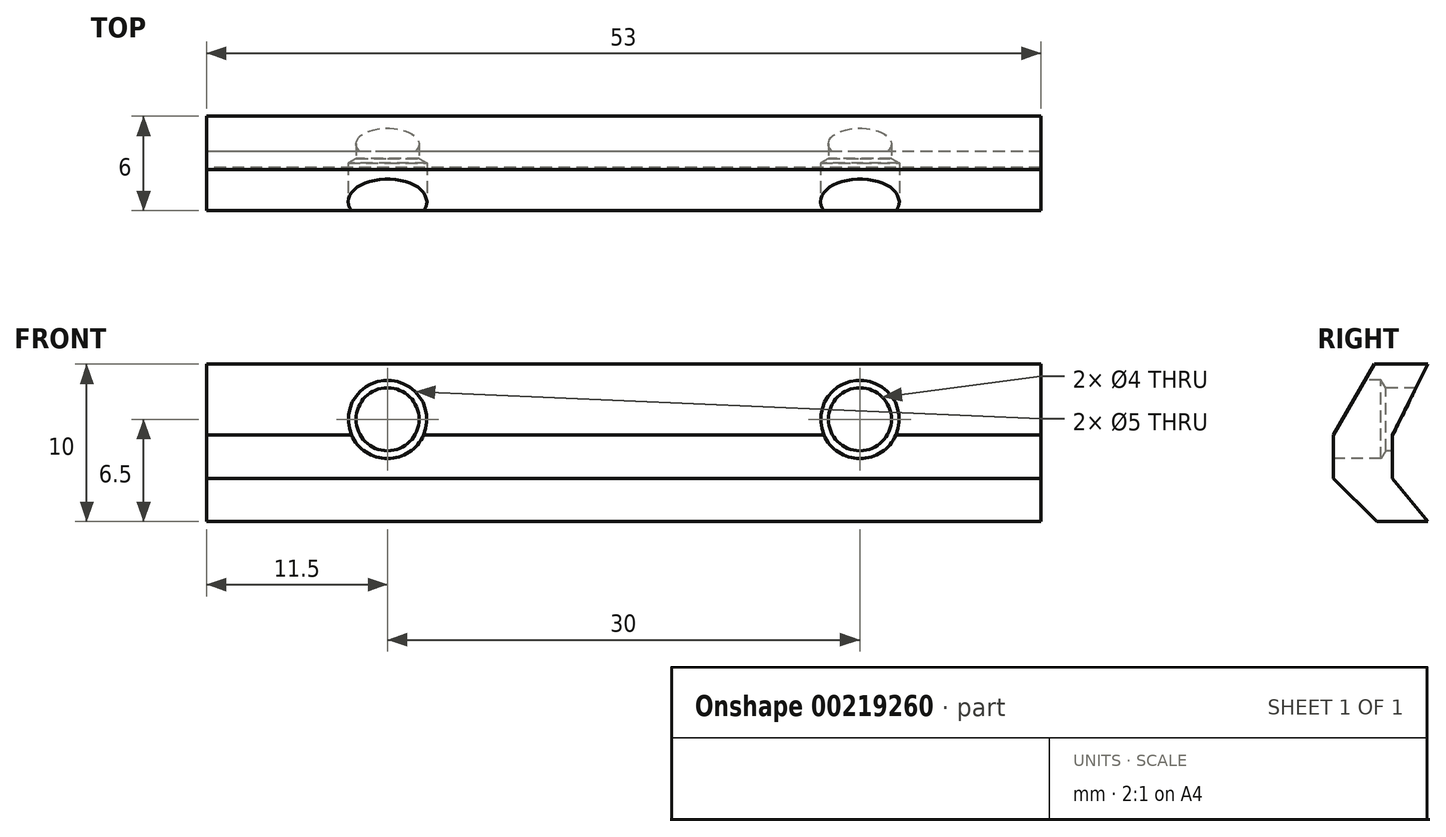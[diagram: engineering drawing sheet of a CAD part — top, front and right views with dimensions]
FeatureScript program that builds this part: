
annotation { "Feature Type Name" : "Feature", "Feature Type Description" : "" }
export const myFeature = defineFeature(function(context is Context, id is Id, definition is map)
    precondition{}
    {
        {
            var Q0;
            Q0=qCreatedBy(makeId("Right.planeOp"),FACE);
            var sketch = newSketch(context, id + "F0", { "sketchPlane" : qUnion([Q0])});
            skLineSegment(sketch, "E0.bottom", {"start": v(2.75, 0) * mm, "end": v(6, 0) * mm});
            skLineSegment(sketch, "E0.top", {"start": v(2.6, 10) * mm, "end": v(6, 10) * mm});
            skLineSegment(sketch, "E0.left", {"start": v(0, 2.75) * mm, "end": v(0, 5.5) * mm});
            skPoint(sketch, "E1", {"position": v(0, 5.5) * mm});
            skPoint(sketch, "E2", {"position": v(0, 2.75) * mm});
            skLineSegment(sketch, "E3", {"start": v(0, 5.5) * mm, "end": v(2.6, 10) * mm});
            skLineSegment(sketch, "E4", {"start": v(0, 2.75) * mm, "end": v(2.75, 0) * mm});
            skPoint(sketch, "E5", {"position": v(3.75, 5.5) * mm});
            skLineSegment(sketch, "E6", {"start": v(6, 10) * mm, "end": v(3.75, 5.5) * mm});
            skLineSegment(sketch, "E7", {"start": v(3.75, 5.5) * mm, "end": v(3.75, 2.75) * mm});
            skLineSegment(sketch, "E8", {"start": v(3.75, 2.75) * mm, "end": v(6, 0) * mm});
            skPoint(sketch, "E9.orphan", {"position": v(0, 10) * mm});
            skSolve(sketch);
        }
        {
            var Q0;
            Q0=makeQuery(id+"F0.imprint","IMPRINT",FACE,{"disambiguationData":[TD([[makeQuery(id+"F0.imprint","IMPRINT",EDGE,{"derivedFrom":sQuery(id+"F0.wireOp",EDGE,"E0.bottom")}),1.0]])]});
            extrude(context, id + "F1", {"entities" : qUnion([Q0]), "depth" : 53 * mm});
        }
        {
            var Q0;
            Q0=makeQuery(id+"F1.opExtrude","SWEPT_FACE",FACE,{"disambiguationData":[OSD([sQuery(id+"F0.wireOp",EDGE,"E0.left")])]});
            var sketch = newSketch(context, id + "F2", { "sketchPlane" : qUnion([Q0])});
            skPoint(sketch, "E10", {"position": v(26.5, 6.5) * mm});
            skPoint(sketch, "E11", {"position": v(11.5, 6.5) * mm});
            skPoint(sketch, "E12", {"position": v(41.5, 6.5) * mm});
            skSolve(sketch);
        }
        {
            var Q0;
            Q0=sQuery(id+"F2.wireOp",VERTEX,"E11");
            var Q1;
            Q1=makeQuery(id+"F1.opExtrude","SWEPT_BODY",BODY,{"disambiguationData":[OSD([sQuery(id+"F0.wireOp",EDGE,"E0.bottom"),sQuery(id+"F0.wireOp",EDGE,"E0.top"),sQuery(id+"F0.wireOp",EDGE,"E0.left"),sQuery(id+"F0.wireOp",EDGE,"E3"),sQuery(id+"F0.wireOp",EDGE,"E4"),sQuery(id+"F0.wireOp",EDGE,"E6"),sQuery(id+"F0.wireOp",EDGE,"E7"),sQuery(id+"F0.wireOp",EDGE,"E8")])]});
            hole(context, id + "F3", {"style" : HoleStyle.SIMPLE, "endStyle" : HoleEndStyle.BLIND, "holeDiameter" : 4 * mm, "holeDepth" : 7.5 * mm, "locations" : qUnion([Q0]), "scope" : qUnion([Q1])});
        }
        {
            var Q0;
            Q0=sQuery(id+"F2.wireOp",VERTEX,"E12");
            var Q1;
            Q1=makeQuery(id+"F1.opExtrude","SWEPT_BODY",BODY,{"disambiguationData":[OSD([sQuery(id+"F0.wireOp",EDGE,"E0.bottom"),sQuery(id+"F0.wireOp",EDGE,"E0.top"),sQuery(id+"F0.wireOp",EDGE,"E0.left"),sQuery(id+"F0.wireOp",EDGE,"E3"),sQuery(id+"F0.wireOp",EDGE,"E4"),sQuery(id+"F0.wireOp",EDGE,"E6"),sQuery(id+"F0.wireOp",EDGE,"E7"),sQuery(id+"F0.wireOp",EDGE,"E8")])]});
            hole(context, id + "F4", {"style" : HoleStyle.SIMPLE, "endStyle" : HoleEndStyle.BLIND, "holeDiameter" : 4 * mm, "holeDepth" : 7.5 * mm, "locations" : qUnion([Q0]), "scope" : qUnion([Q1])});
        }
        {
            var Q0;
            Q0=sQuery(id+"F2.wireOp",VERTEX,"E11");
            var Q1;
            Q1=makeQuery(id+"F1.opExtrude","SWEPT_BODY",BODY,{"disambiguationData":[OSD([sQuery(id+"F0.wireOp",EDGE,"E0.bottom"),sQuery(id+"F0.wireOp",EDGE,"E0.top"),sQuery(id+"F0.wireOp",EDGE,"E0.left"),sQuery(id+"F0.wireOp",EDGE,"E3"),sQuery(id+"F0.wireOp",EDGE,"E4"),sQuery(id+"F0.wireOp",EDGE,"E6"),sQuery(id+"F0.wireOp",EDGE,"E7"),sQuery(id+"F0.wireOp",EDGE,"E8")])]});
            hole(context, id + "F5", {"style" : HoleStyle.SIMPLE, "endStyle" : HoleEndStyle.BLIND, "holeDiameter" : 5 * mm, "holeDepth" : 1 * mm, "locations" : qUnion([Q0]), "scope" : qUnion([Q1])});
        }
        {
            var Q0;
            Q0=sQuery(id+"F2.wireOp",VERTEX,"E12");
            var Q1;
            Q1=makeQuery(id+"F1.opExtrude","SWEPT_BODY",BODY,{"disambiguationData":[OSD([sQuery(id+"F0.wireOp",EDGE,"E0.bottom"),sQuery(id+"F0.wireOp",EDGE,"E0.top"),sQuery(id+"F0.wireOp",EDGE,"E0.left"),sQuery(id+"F0.wireOp",EDGE,"E3"),sQuery(id+"F0.wireOp",EDGE,"E4"),sQuery(id+"F0.wireOp",EDGE,"E6"),sQuery(id+"F0.wireOp",EDGE,"E7"),sQuery(id+"F0.wireOp",EDGE,"E8")])]});
            hole(context, id + "F6", {"style" : HoleStyle.SIMPLE, "endStyle" : HoleEndStyle.BLIND, "holeDiameter" : 5 * mm, "holeDepth" : 1 * mm, "locations" : qUnion([Q0]), "scope" : qUnion([Q1])});
        }
    });
